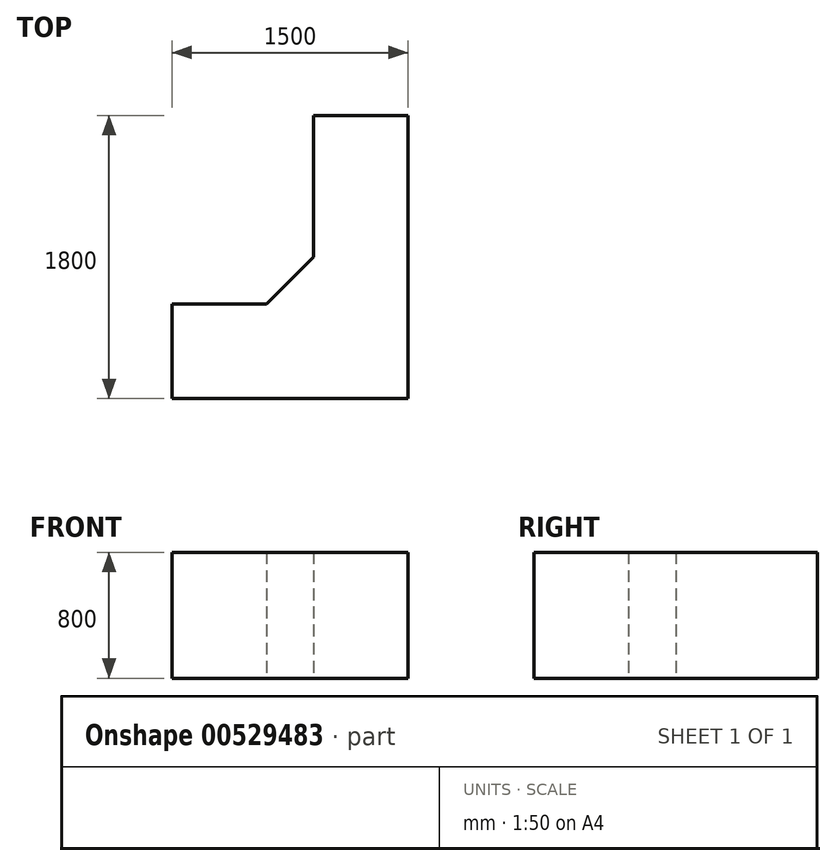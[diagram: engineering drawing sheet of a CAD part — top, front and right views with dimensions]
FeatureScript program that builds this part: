
annotation { "Feature Type Name" : "Feature", "Feature Type Description" : "" }
export const myFeature = defineFeature(function(context is Context, id is Id, definition is map)
    precondition{}
    {
        {
            var Q0;
            Q0=qCreatedBy(makeId("Top.planeOp"),FACE);
            var sketch = newSketch(context, id + "F0", { "sketchPlane" : qUnion([Q0])});
            skLineSegment(sketch, "E0", {"start": v(0, 0) * mm, "end": v(-1500, 0) * mm});
            skLineSegment(sketch, "E1", {"start": v(-1500, 0) * mm, "end": v(-1500, 600) * mm});
            skLineSegment(sketch, "E2", {"start": v(-1500, 600) * mm, "end": v(-900, 600) * mm});
            skLineSegment(sketch, "E3", {"start": v(-900, 600) * mm, "end": v(-600, 900) * mm});
            skLineSegment(sketch, "E4", {"start": v(-600, 900) * mm, "end": v(-600, 1800) * mm});
            skLineSegment(sketch, "E5", {"start": v(-600, 1800) * mm, "end": v(0, 1800) * mm});
            skLineSegment(sketch, "E6", {"start": v(0, 1800) * mm, "end": v(0, 0) * mm});
            skSolve(sketch);
        }
        {
            var Q0;
            Q0=makeQuery(id+"F0.imprint","IMPRINT",FACE,{"disambiguationData":[TD([[makeQuery(id+"F0.imprint","IMPRINT",EDGE,{"derivedFrom":sQuery(id+"F0.wireOp",EDGE,"E0")}),-1.0]])]});
            extrude(context, id + "F1", {"entities" : qUnion([Q0]), "depth" : 800 * mm, "offsetDistance" : 25 * mm});
        }
    });
